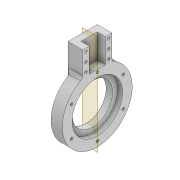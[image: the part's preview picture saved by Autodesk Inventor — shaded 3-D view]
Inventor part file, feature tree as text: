
AUTODESK INVENTOR PART (.ipt)
format: ipt  version: 2022 (Build 260153000, 153)  size: 213,504 bytes
history: native  units: mm
features: extrude x7, sketch x6, fillet x2, pattern_circular x1, plane x1, mirror x1, projected_geometry x1
ambient origin geometry x8: Origin, YZ Plane, XZ Plane, XY Plane, X Axis, Y Axis, Z Axis, Center Point
bodies: Solid1 (feature_tree)
feature tree (19):
  extrude  "Extrusion1"  Depth=12.0mm
  extrude  "Extrusion2"  Depth=8.0mm TaperAngle=0.0deg
  extrude  "Extrusion3"  Depth=6.0mm TaperAngle=0.0deg
  pattern_circular  "Circular Pattern1"  Count=10  [1 undecoded]
  plane  "Work Plane1"
  sketch  "Sketch4"  dims[d8=3.2mm]
  extrude  "Extrusion4"  Depth=5.0mm
  extrude  "Extrusion5"  Depth=10.1mm
  fillet  "Fillet1"  Radius=20.2mm
  extrude  "Extrusion6"  Depth=10.1mm
  fillet  "Fillet2"  Radius=8.0mm
  extrude  "Extrusion7"  Depth=8.0mm
  mirror  "Mirror1"
  sketch  "Sketch1"  dims[d0=62.5mm d1=12.0mm]
  sketch  "Sketch2"  dims[d2=50.0mm d3=8.0mm d4=0.0mm]
  projected_geometry  "Projected Loop1"
  sketch  "Sketch3"  dims[d5=62.5mm d6=6.0mm d7=0.0mm]
  sketch  "Sketch6"  dims[d9=37.0mm d10=100.0mm d11=0.0mm]
  sketch  "Sketch7"  dims[d12=60.0mm d13=360.0deg d15=40.0mm d16=10.1mm d17=20.2mm d18=10.1mm d20=8.0mm d21=8.0mm d22=100.0mm d23=0.0mm d24=30.0mm d25=0.0mm d26=5.0mm d27=3.2mm d28=3.2mm d29=3.2mm d30=4.0mm d31=4.0mm d32=15.0mm d33=4.0mm d34=9.0mm d35=4.0mm d36=0.0mm d37=5.0mm d38=100.0mm d39=0.0mm]
note: 1 required parameter value undecoded (feature->parameter linkage not recoverable at this tier; creation-order binding heuristic only, values carry confidence <= 0.55)
